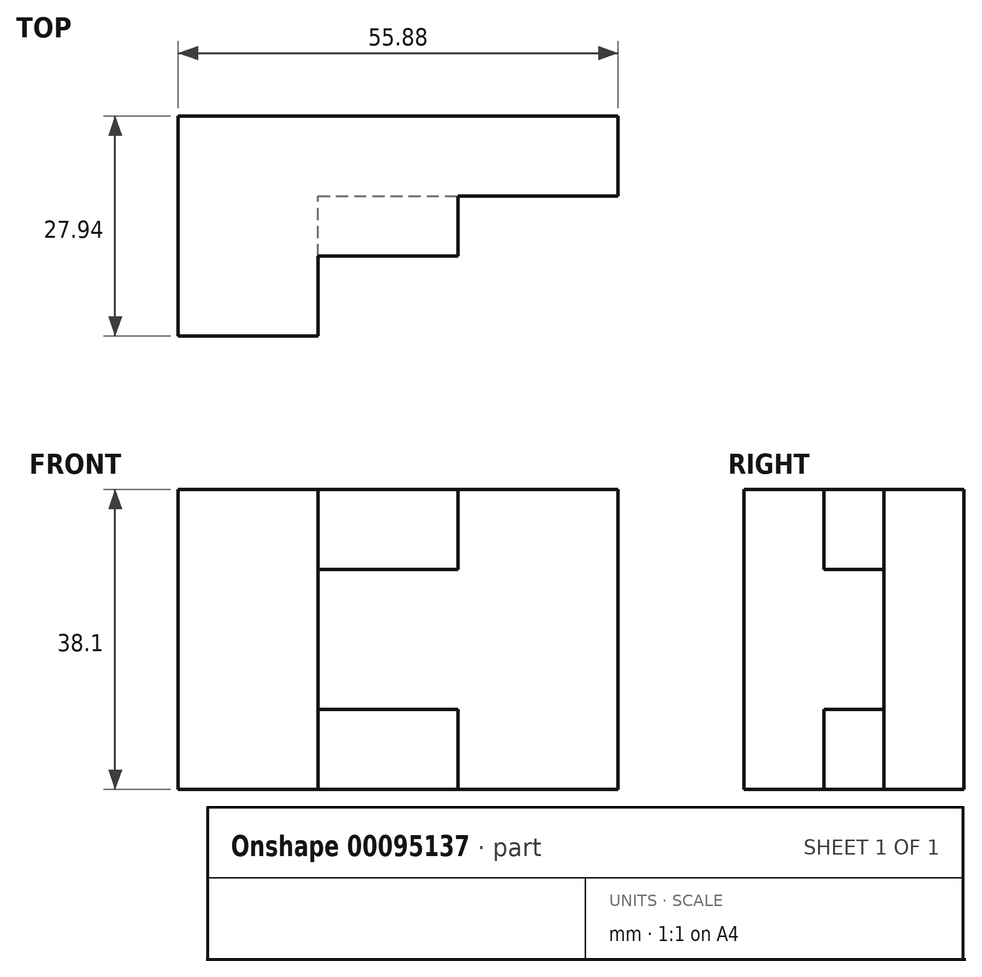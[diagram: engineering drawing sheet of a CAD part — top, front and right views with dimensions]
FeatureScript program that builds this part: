
annotation { "Feature Type Name" : "Feature", "Feature Type Description" : "" }
export const myFeature = defineFeature(function(context is Context, id is Id, definition is map)
    precondition{}
    {
        {
            var Q0;
            Q0=qCreatedBy(makeId("Front.planeOp"),FACE);
            var sketch = newSketch(context, id + "F0", { "sketchPlane" : qUnion([Q0])});
            skLineSegment(sketch, "E0.bottom", {"start": v(-27.94, 19.05) * mm, "end": v(27.94, 19.05) * mm});
            skLineSegment(sketch, "E0.top", {"start": v(-27.94, -19.05) * mm, "end": v(27.94, -19.05) * mm});
            skLineSegment(sketch, "E0.left", {"start": v(-27.94, 19.05) * mm, "end": v(-27.94, -19.05) * mm});
            skLineSegment(sketch, "E0.right", {"start": v(27.94, 19.05) * mm, "end": v(27.94, -19.05) * mm});
            skPoint(sketch, "E0.middle", {"position": v(0, 0) * mm});
            skSolve(sketch);
        }
        {
            var Q0;
            Q0 = qSketchRegion(id + "F0", true);
            extrude(context, id + "F1", {"entities" : qUnion([Q0]), "depth" : 10.16 * mm});
        }
        {
            var Q0;
            Q0=makeQuery(id+"F1.opExtrude","CAP_FACE",FACE,{"disambiguationData":[OSD([sQuery(id+"F0.wireOp",EDGE,"E0.bottom"),sQuery(id+"F0.wireOp",EDGE,"E0.top"),sQuery(id+"F0.wireOp",EDGE,"E0.left"),sQuery(id+"F0.wireOp",EDGE,"E0.right")])],"isStart":false});
            var sketch = newSketch(context, id + "F2", { "sketchPlane" : qUnion([Q0])});
            skLineSegment(sketch, "E1.bottom", {"start": v(-27.94, 19.05) * mm, "end": v(-10.16, 19.05) * mm});
            skLineSegment(sketch, "E1.top", {"start": v(-27.94, -19.05) * mm, "end": v(-10.16, -19.05) * mm});
            skLineSegment(sketch, "E1.left", {"start": v(-27.94, 19.05) * mm, "end": v(-27.94, -19.05) * mm});
            skLineSegment(sketch, "E1.right", {"start": v(-10.16, 19.05) * mm, "end": v(-10.16, -19.05) * mm});
            skSolve(sketch);
        }
        {
            var Q0;
            Q0 = qSketchRegion(id + "F2", true);
            extrude(context, id + "F3", {"entities" : qUnion([Q0]), "operationType" : NewBodyOperationType.ADD, "depth" : 17.78 * mm});
        }
        {
            var Q0;
            Q0=makeQuery(id+"F1.opExtrude","CAP_FACE",FACE,{"disambiguationData":[OSD([sQuery(id+"F0.wireOp",EDGE,"E0.bottom"),sQuery(id+"F0.wireOp",EDGE,"E0.top"),sQuery(id+"F0.wireOp",EDGE,"E0.left"),sQuery(id+"F0.wireOp",EDGE,"E0.right")])],"isStart":false});
            var sketch = newSketch(context, id + "F4", { "sketchPlane" : qUnion([Q0])});
            skLineSegment(sketch, "E2.bottom", {"start": v(-10.16, 19.05) * mm, "end": v(7.62, 19.05) * mm});
            skLineSegment(sketch, "E2.top", {"start": v(-10.16, 8.9) * mm, "end": v(7.62, 8.9) * mm});
            skLineSegment(sketch, "E2.left", {"start": v(-10.16, 19.05) * mm, "end": v(-10.16, 8.9) * mm});
            skLineSegment(sketch, "E2.right", {"start": v(7.62, 19.05) * mm, "end": v(7.62, 8.9) * mm});
            skLineSegment(sketch, "E3.bottom", {"start": v(-10.16, -19.05) * mm, "end": v(7.62, -19.05) * mm});
            skLineSegment(sketch, "E3.top", {"start": v(-10.16, -8.9) * mm, "end": v(7.62, -8.9) * mm});
            skLineSegment(sketch, "E3.left", {"start": v(-10.16, -19.05) * mm, "end": v(-10.16, -8.9) * mm});
            skLineSegment(sketch, "E3.right", {"start": v(7.62, -19.05) * mm, "end": v(7.62, -8.9) * mm});
            skSolve(sketch);
        }
        {
            var Q0;
            Q0 = qSketchRegion(id + "F4", true);
            extrude(context, id + "F5", {"entities" : qUnion([Q0]), "operationType" : NewBodyOperationType.ADD, "depth" : 7.62 * mm});
        }
    });
